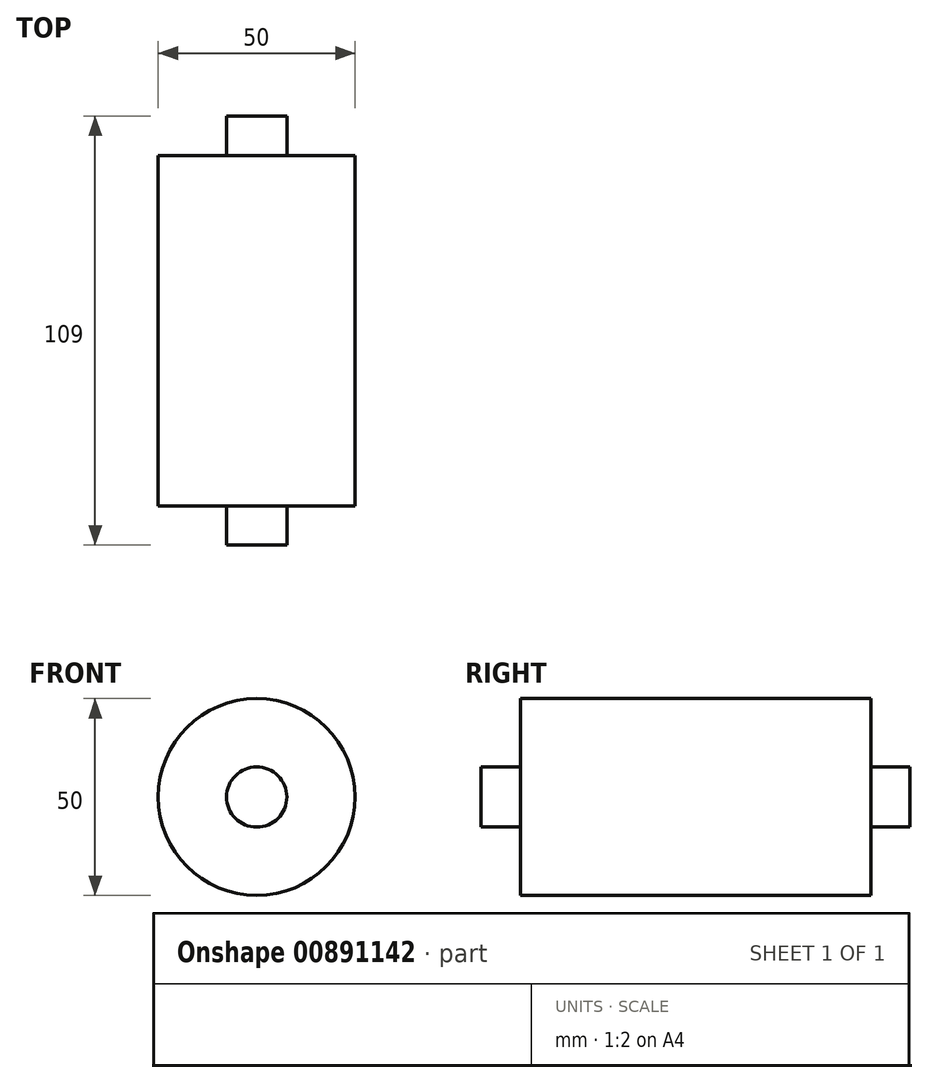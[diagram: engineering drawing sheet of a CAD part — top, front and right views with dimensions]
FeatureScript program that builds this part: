
annotation { "Feature Type Name" : "Feature", "Feature Type Description" : "" }
export const myFeature = defineFeature(function(context is Context, id is Id, definition is map)
    precondition{}
    {
        {
            var Q0;
            Q0=qCreatedBy(makeId("Front.planeOp"),FACE);
            var sketch = newSketch(context, id + "F0", { "sketchPlane" : qUnion([Q0])});
            skCircle(sketch, "E0", {"center": v(0, 0) * mm, "radius": 25 * mm});
            skSolve(sketch);
        }
        {
            var Q0;
            Q0 = qSketchRegion(id + "F0", true);
            extrude(context, id + "F1", {"entities" : qUnion([Q0]), "endBound" : BoundingType.SYMMETRIC, "depth" : 89 * mm, "offsetDistance" : 25 * mm});
        }
        {
            var Q0;
            Q0=makeQuery(id+"F1.opExtrude","CAP_FACE",FACE,{"disambiguationData":[OSD([sQuery(id+"F0.wireOp",EDGE,"E0")])],"isStart":false});
            var sketch = newSketch(context, id + "F2", { "sketchPlane" : qUnion([Q0])});
            skCircle(sketch, "E1", {"center": v(0, 0) * mm, "radius": 7.65 * mm});
            skSolve(sketch);
        }
        {
            var Q0;
            Q0 = qSketchRegion(id + "F2", true);
            extrude(context, id + "F3", {"entities" : qUnion([Q0]), "operationType" : NewBodyOperationType.ADD, "depth" : 10 * mm, "offsetDistance" : 25 * mm});
        }
        {
            var Q0;
            Q0=makeQuery(id+"F1.opExtrude","CAP_FACE",FACE,{"disambiguationData":[OSD([sQuery(id+"F0.wireOp",EDGE,"E0")])],"isStart":true});
            var sketch = newSketch(context, id + "F4", { "sketchPlane" : qUnion([Q0])});
            skCircle(sketch, "E2", {"center": v(0, 0) * mm, "radius": 7.65 * mm});
            skSolve(sketch);
        }
        {
            var Q0;
            Q0 = qSketchRegion(id + "F4", true);
            extrude(context, id + "F5", {"entities" : qUnion([Q0]), "operationType" : NewBodyOperationType.ADD, "depth" : 10 * mm, "offsetDistance" : 25 * mm});
        }
    });
